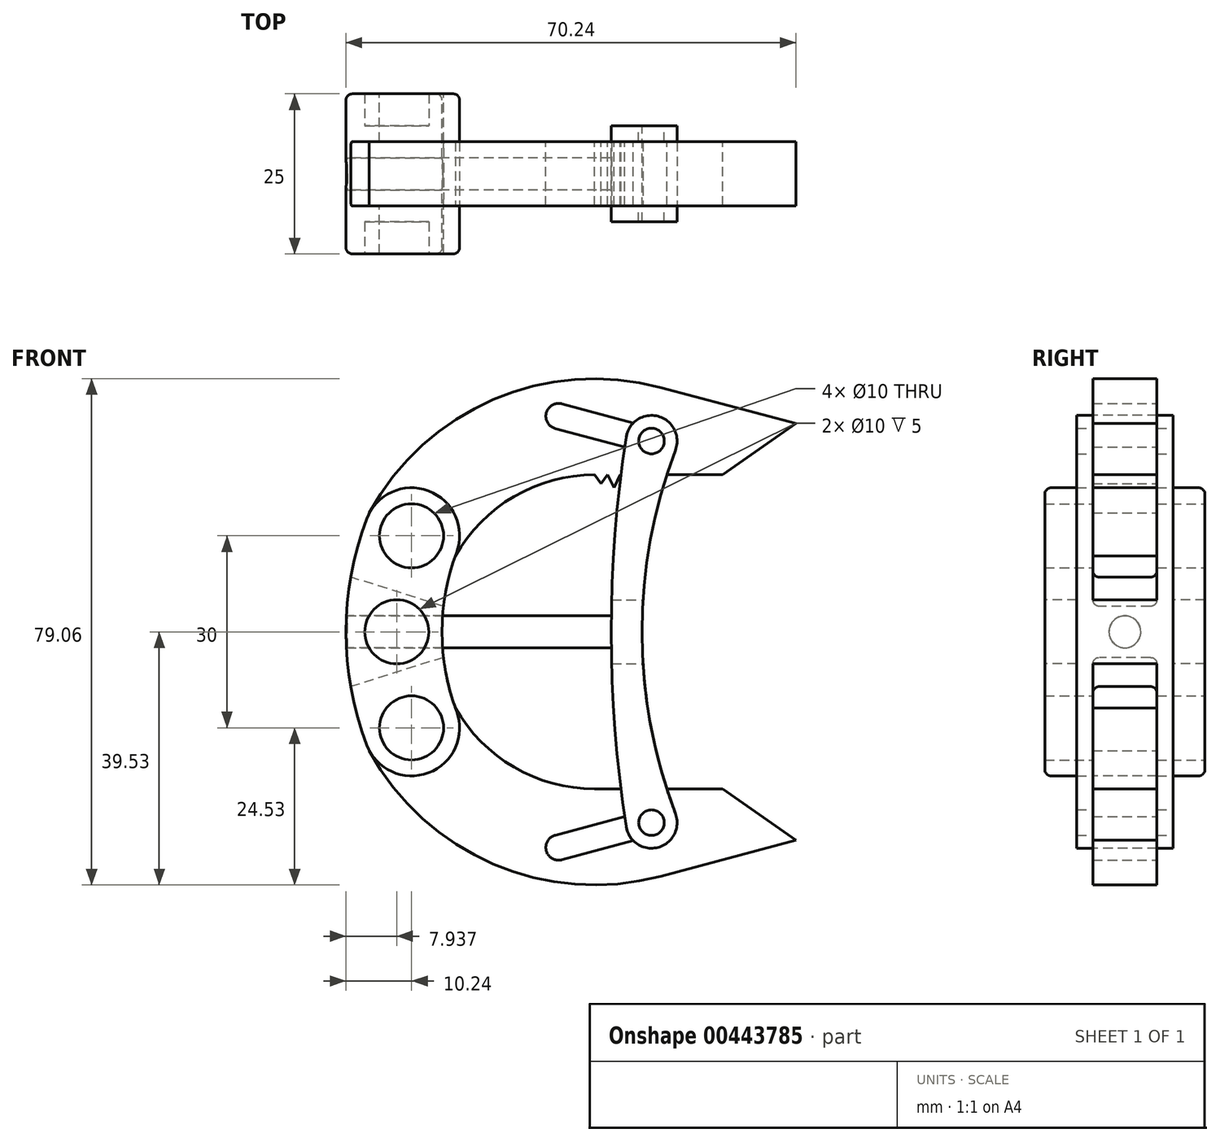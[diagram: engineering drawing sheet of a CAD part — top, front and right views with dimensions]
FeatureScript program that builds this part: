
annotation { "Feature Type Name" : "Feature", "Feature Type Description" : "" }
export const myFeature = defineFeature(function(context is Context, id is Id, definition is map)
    precondition{}
    {
        {
            var Q0;
            Q0=qCreatedBy(makeId("Front.planeOp"),FACE);
            var sketch = newSketch(context, id + "F0", { "sketchPlane" : qUnion([Q0])});
            skLineSegment(sketch, "E0", {"start": v(0, 15) * mm, "end": v(0, -15) * mm, "construction": true});
            skLineSegment(sketch, "E1", {"start": v(0, 0) * mm, "end": v(80, 0) * mm, "construction": true});
            skCircle(sketch, "E2", {"center": v(0, 15) * mm, "radius": 5 * mm});
            skCircle(sketch, "E3", {"center": v(0, -15) * mm, "radius": 5 * mm});
            skArc(sketch, "E4.0", {"start": v(7.02, 12.35) * mm, "mid": v(2.65, 22.02) * mm, "end": v(-7.02, 17.65) * mm});
            skArc(sketch, "E5.0", {"start": v(-7.02, -17.65) * mm, "mid": v(2.65, -22.02) * mm, "end": v(7.02, -12.35) * mm});
            skArc(sketch, "E6", {"start": v(-7.02, 17.65) * mm, "mid": v(-10.24, 0) * mm, "end": v(-7.02, -17.65) * mm});
            skArc(sketch, "E7", {"start": v(7.02, 12.35) * mm, "mid": v(4.76, 0) * mm, "end": v(7.02, -12.35) * mm});
            skSolve(sketch);
        }
        {
            var Q0;
            Q0=qCreatedBy(makeId("Front.planeOp"),FACE);
            var sketch = newSketch(context, id + "F1", { "sketchPlane" : qUnion([Q0])});
            skCircle(sketch, "E8.0", {"center": v(0, 15) * mm, "radius": 5 * mm});
            skArc(sketch, "E9", {"start": v(-6.6, 18.57) * mm, "mid": v(-3.57, 8.4) * mm, "end": v(6.6, 11.43) * mm});
            skArc(sketch, "E10", {"start": v(38.92, 38.17) * mm, "mid": v(12.76, 36.27) * mm, "end": v(-6.6, 18.57) * mm});
            skLineSegment(sketch, "E11", {"start": v(38.92, 38.17) * mm, "end": v(60, 32.53) * mm});
            skLineSegment(sketch, "E12", {"start": v(60, 32.53) * mm, "end": v(48.58, 24.53) * mm});
            skLineSegment(sketch, "E13", {"start": v(48.58, 24.53) * mm, "end": v(28.58, 24.53) * mm});
            skArc(sketch, "E14", {"start": v(28.58, 24.53) * mm, "mid": v(15.79, 21) * mm, "end": v(6.6, 11.43) * mm});
            skLineSegment(sketch, "E15", {"start": v(38.92, 38.17) * mm, "end": v(37.45, 29.8) * mm, "construction": true});
            skLineSegment(sketch, "E16", {"start": v(37.45, 29.8) * mm, "end": v(22.96, 33.68) * mm, "construction": true});
            skArc(sketch, "E17", {"start": v(23.48, 35.6) * mm, "mid": v(21.03, 34.2) * mm, "end": v(22.44, 31.75) * mm});
            skArc(sketch, "E18", {"start": v(36.93, 27.87) * mm, "mid": v(39.4, 29.37) * mm, "end": v(37.8, 31.77) * mm});
            skLineSegment(sketch, "E19", {"start": v(22.44, 31.75) * mm, "end": v(36.93, 27.87) * mm});
            skLineSegment(sketch, "E20", {"start": v(23.48, 35.6) * mm, "end": v(37.97, 31.73) * mm});
            skLineSegment(sketch, "E21.MirrorCS", {"start": v(23.48, -35.6) * mm, "end": v(37.97, -31.73) * mm});
            skLineSegment(sketch, "E22.MirrorCS", {"start": v(60, -32.53) * mm, "end": v(48.58, -24.53) * mm});
            skArc(sketch, "E23.MirrorCS", {"start": v(28.58, -24.53) * mm, "mid": v(15.79, -21) * mm, "end": v(6.6, -11.43) * mm});
            skLineSegment(sketch, "E24.MirrorCS", {"start": v(38.92, -38.17) * mm, "end": v(37.45, -29.8) * mm, "construction": true});
            skArc(sketch, "E25.MirrorC", {"start": v(-6.6, -18.57) * mm, "mid": v(-3.57, -8.4) * mm, "end": v(6.6, -11.43) * mm});
            skArc(sketch, "E26.MirrorCS", {"start": v(23.48, -35.6) * mm, "mid": v(21.03, -34.2) * mm, "end": v(22.44, -31.75) * mm});
            skLineSegment(sketch, "E27.MirrorCS", {"start": v(38.92, -38.17) * mm, "end": v(60, -32.53) * mm});
            skLineSegment(sketch, "E28.MirrorCS", {"start": v(22.44, -31.75) * mm, "end": v(36.93, -27.87) * mm});
            skLineSegment(sketch, "E29.MirrorCS", {"start": v(37.45, -29.8) * mm, "end": v(22.96, -33.68) * mm, "construction": true});
            skCircle(sketch, "E30.MirrorC", {"center": v(0, -15) * mm, "radius": 5 * mm});
            skArc(sketch, "E31.MirrorCS", {"start": v(38.92, -38.17) * mm, "mid": v(12.76, -36.27) * mm, "end": v(-6.6, -18.57) * mm});
            skArc(sketch, "E32.MirrorCS", {"start": v(36.93, -27.87) * mm, "mid": v(39.4, -29.37) * mm, "end": v(37.8, -31.77) * mm});
            skLineSegment(sketch, "E33.MirrorCS", {"start": v(48.58, -24.53) * mm, "end": v(28.58, -24.53) * mm});
            skLineSegment(sketch, "E34", {"start": v(28.58, 24.53) * mm, "end": v(29.6, 23.14) * mm});
            skLineSegment(sketch, "E35", {"start": v(29.6, 23.14) * mm, "end": v(30.58, 24.53) * mm});
            skLineSegment(sketch, "E36", {"start": v(30.58, 24.53) * mm, "end": v(31.6, 22.53) * mm});
            skLineSegment(sketch, "E37", {"start": v(31.6, 22.53) * mm, "end": v(32.58, 24.53) * mm});
            skLineSegment(sketch, "E38.1.0.0", {"start": v(32.6, 24.2) * mm, "end": v(33.62, 22.82) * mm});
            skLineSegment(sketch, "E38.1.0.1", {"start": v(33.62, 22.82) * mm, "end": v(34.6, 24.2) * mm});
            skLineSegment(sketch, "E38.1.0.2", {"start": v(34.6, 24.2) * mm, "end": v(35.62, 22.2) * mm});
            skLineSegment(sketch, "E38.1.0.3", {"start": v(35.62, 22.2) * mm, "end": v(36.6, 24.2) * mm});
            skLineSegment(sketch, "E38.2.0.0", {"start": v(36.63, 23.89) * mm, "end": v(37.64, 22.5) * mm});
            skLineSegment(sketch, "E38.2.0.1", {"start": v(37.64, 22.5) * mm, "end": v(38.63, 23.89) * mm});
            skLineSegment(sketch, "E38.2.0.2", {"start": v(38.63, 23.89) * mm, "end": v(39.64, 21.89) * mm});
            skLineSegment(sketch, "E38.2.0.3", {"start": v(39.64, 21.89) * mm, "end": v(40.63, 23.89) * mm});
            skLineSegment(sketch, "E38.3.0.0", {"start": v(40.66, 23.57) * mm, "end": v(41.67, 22.17) * mm});
            skLineSegment(sketch, "E38.3.0.1", {"start": v(41.67, 22.17) * mm, "end": v(42.66, 23.57) * mm});
            skLineSegment(sketch, "E38.3.0.2", {"start": v(42.66, 23.57) * mm, "end": v(43.67, 21.57) * mm});
            skLineSegment(sketch, "E38.3.0.3", {"start": v(43.67, 21.57) * mm, "end": v(44.66, 23.57) * mm});
            skLineSegment(sketch, "E38.4.0.0", {"start": v(44.68, 23.24) * mm, "end": v(45.7, 21.85) * mm});
            skLineSegment(sketch, "E38.4.0.1", {"start": v(45.7, 21.85) * mm, "end": v(46.68, 23.24) * mm});
            skLineSegment(sketch, "E38.4.0.2", {"start": v(46.68, 23.24) * mm, "end": v(47.7, 21.24) * mm});
            skLineSegment(sketch, "E38.4.0.3", {"start": v(47.7, 21.24) * mm, "end": v(48.68, 23.24) * mm});
            skLineSegment(sketch, "E38.direction1", {"start": v(29.6, 23.14) * mm, "end": v(33.62, 22.82) * mm, "construction": true});
            skSolve(sketch);
        }
        {
            var Q0;
            Q0 = qSketchRegion(id + "F1", true);
            extrude(context, id + "F2", {"entities" : qUnion([Q0]), "endBound" : BoundingType.SYMMETRIC, "depth" : 10 * mm});
        }
        {
            var Q0;
            Q0 = qSketchRegion(id + "F0", true);
            extrude(context, id + "F3", {"entities" : qUnion([Q0]), "endBound" : BoundingType.SYMMETRIC, "depth" : 25 * mm});
        }
        {
            var Q0;
            Q0=makeQuery(id+"F3.opExtrude","CAP_FACE",FACE,{"disambiguationData":[OSD([sQuery(id+"F0.wireOp",EDGE,"E2"),sQuery(id+"F0.wireOp",EDGE,"E3"),sQuery(id+"F0.wireOp",EDGE,"E4.0"),sQuery(id+"F0.wireOp",EDGE,"E5.0"),sQuery(id+"F0.wireOp",EDGE,"E6"),sQuery(id+"F0.wireOp",EDGE,"E7")])],"isStart":false});
            var sketch = newSketch(context, id + "F4", { "sketchPlane" : qUnion([Q0])});
            skArc(sketch, "E39", {"start": v(0, 15) * mm, "mid": v(-2.3, 0) * mm, "end": v(0, -15) * mm, "construction": true});
            skCircle(sketch, "E40", {"center": v(-2.3, 0) * mm, "radius": 5 * mm});
            skSolve(sketch);
        }
        {
            var Q0;
            Q0 = qSketchRegion(id + "F4", true);
            extrude(context, id + "F5", {"entities" : qUnion([Q0]), "operationType" : NewBodyOperationType.REMOVE, "endBound" : BoundingType.THROUGH_ALL, "oppositeDirection" : true, "depth" : 25 * mm});
        }
        {
            var Q0;
            Q0=qCreatedBy(makeId("Front.planeOp"),FACE);
            var sketch = newSketch(context, id + "F6", { "sketchPlane" : qUnion([Q0])});
            skArc(sketch, "E41.0", {"start": v(7.02, 12.35) * mm, "mid": v(2.65, 22.02) * mm, "end": v(-7.02, 17.65) * mm});
            skArc(sketch, "E41.1", {"start": v(-7.02, 17.65) * mm, "mid": v(-8.47, 13.16) * mm, "end": v(-9.5, 8.55) * mm});
            skCircle(sketch, "E41.2", {"center": v(0, 15) * mm, "radius": 5 * mm});
            skArc(sketch, "E41.3", {"start": v(7.02, 12.35) * mm, "mid": v(5.75, 8.24) * mm, "end": v(5, 4) * mm});
            skCircle(sketch, "E41.4", {"center": v(-2.3, 0) * mm, "radius": 5 * mm});
            skCircle(sketch, "E41.5", {"center": v(0, -15) * mm, "radius": 5 * mm});
            skArc(sketch, "E41.6", {"start": v(-7.02, -17.65) * mm, "mid": v(2.65, -22.02) * mm, "end": v(7.02, -12.35) * mm});
            skCircle(sketch, "E42.0", {"center": v(-2.3, 0) * mm, "radius": 6 * mm, "construction": true});
            skCircle(sketch, "E43", {"center": v(0, -15) * mm, "radius": 9 * mm, "construction": true});
            skLineSegment(sketch, "E44", {"start": v(5, -4) * mm, "end": v(5, -4) * mm});
            skLineSegment(sketch, "E45", {"start": v(5, 4) * mm, "end": v(-9.5, 8.55) * mm});
            skLineSegment(sketch, "E46", {"start": v(-2.3, 0) * mm, "end": v(19.17, 0) * mm, "construction": true});
            skArc(sketch, "E47", {"start": v(-9.5, 8.55) * mm, "mid": v(-10.24, 0) * mm, "end": v(-9.5, -8.55) * mm, "construction": true});
            skArc(sketch, "E48", {"start": v(-9.5, -8.55) * mm, "mid": v(-8.47, -13.16) * mm, "end": v(-7.02, -17.65) * mm});
            skLineSegment(sketch, "E49", {"start": v(5, -4) * mm, "end": v(-9.5, -8.55) * mm});
            skArc(sketch, "E50", {"start": v(5, 4) * mm, "mid": v(4.76, 0) * mm, "end": v(5, -4) * mm, "construction": true});
            skArc(sketch, "E51", {"start": v(5, -4) * mm, "mid": v(5.75, -8.24) * mm, "end": v(7.02, -12.35) * mm});
            skSolve(sketch);
        }
        {
            var Q0;
            Q0 = qSketchRegion(id + "F6", true);
            extrude(context, id + "F7", {"entities" : qUnion([Q0]), "operationType" : NewBodyOperationType.REMOVE, "endBound" : BoundingType.SYMMETRIC, "oppositeDirection" : true, "depth" : 10 * mm});
        }
        {
            var Q0;
            Q0=qCreatedBy(makeId("Front.planeOp"),FACE);
            var sketch = newSketch(context, id + "F8", { "sketchPlane" : qUnion([Q0])});
            skCircle(sketch, "E52.1.0", {"center": v(-2.3, 0) * mm, "radius": 5 * mm});
            skSolve(sketch);
        }
        {
            var Q0;
            Q0 = qSketchRegion(id + "F8", true);
            extrude(context, id + "F9", {"entities" : qUnion([Q0]), "operationType" : NewBodyOperationType.ADD, "endBound" : BoundingType.SYMMETRIC, "depth" : 15 * mm});
        }
        {
            var Q0;
            Q0=qCreatedBy(makeId("Right.planeOp"),FACE);
            var sketch = newSketch(context, id + "F10", { "sketchPlane" : qUnion([Q0])});
            skCircle(sketch, "E53", {"center": v(0, 0) * mm, "radius": 2.5 * mm});
            skSolve(sketch);
        }
        {
            var Q0;
            Q0 = qSketchRegion(id + "F10", true);
            extrude(context, id + "F11", {"entities" : qUnion([Q0]), "operationType" : NewBodyOperationType.REMOVE, "endBound" : BoundingType.THROUGH_ALL, "oppositeDirection" : true, "depth" : 25 * mm, "hasSecondDirection" : true, "secondDirectionBound" : SecondDirectionBoundingType.THROUGH_ALL, "secondDirectionOppositeDirection" : false, "secondDirectionDepth" : 25 * mm});
        }
        {
            var Q0;
            Q0=qCreatedBy(makeId("Right.planeOp"),FACE);
            var sketch = newSketch(context, id + "F12", { "sketchPlane" : qUnion([Q0])});
            skCircle(sketch, "E54.0", {"center": v(0, 0) * mm, "radius": 2.5 * mm});
            skSolve(sketch);
        }
        {
            var Q0;
            Q0 = qSketchRegion(id + "F12", true);
            extrude(context, id + "F13", {"entities" : qUnion([Q0]), "depth" : 32 * mm, "hasSecondDirection" : true, "secondDirectionOppositeDirection" : true, "secondDirectionDepth" : 10 * mm});
        }
        {
            var Q0;
            Q0=qCreatedBy(makeId("Front.planeOp"),FACE);
            var sketch = newSketch(context, id + "F14", { "sketchPlane" : qUnion([Q0])});
            skArc(sketch, "E55.0", {"start": v(36.93, 27.87) * mm, "mid": v(39.38, 29.28) * mm, "end": v(37.97, 31.73) * mm});
            skArc(sketch, "E55.1", {"start": v(36.93, -27.87) * mm, "mid": v(39.38, -29.28) * mm, "end": v(37.97, -31.73) * mm});
            skCircle(sketch, "E56", {"center": v(37.45, 29.8) * mm, "radius": 2 * mm});
            skCircle(sketch, "E57", {"center": v(37.45, -29.8) * mm, "radius": 2 * mm});
            skCircle(sketch, "E58", {"center": v(37.45, 29.8) * mm, "radius": 4 * mm});
            skCircle(sketch, "E59", {"center": v(37.45, -29.8) * mm, "radius": 4 * mm});
            skArc(sketch, "E60", {"start": v(33.5, 30.4) * mm, "mid": v(31.17, 0) * mm, "end": v(33.5, -30.4) * mm});
            skArc(sketch, "E61", {"start": v(41.19, 28.38) * mm, "mid": v(35.99, 0) * mm, "end": v(41.19, -28.38) * mm});
            skSolve(sketch);
        }
        {
            var Q0;
            Q0 = qSketchRegion(id + "F14", true);
            extrude(context, id + "F15", {"entities" : qUnion([Q0]), "operationType" : NewBodyOperationType.ADD, "endBound" : BoundingType.SYMMETRIC, "depth" : 15 * mm});
        }
        {
            var Q0;
            Q0=qCreatedBy(makeId("Front.planeOp"),FACE);
            var sketch = newSketch(context, id + "F16", { "sketchPlane" : qUnion([Q0])});
            skArc(sketch, "E62.0", {"start": v(33.5, 30.4) * mm, "mid": v(31.96, 17.74) * mm, "end": v(31.23, 5) * mm});
            skArc(sketch, "E62.1", {"start": v(41.19, 28.38) * mm, "mid": v(38.47, 33.67) * mm, "end": v(33.5, 30.4) * mm});
            skArc(sketch, "E62.2", {"start": v(33.5, -30.4) * mm, "mid": v(38.47, -33.67) * mm, "end": v(41.19, -28.38) * mm});
            skArc(sketch, "E62.3", {"start": v(41.19, 28.38) * mm, "mid": v(37.79, 16.88) * mm, "end": v(36.14, 5) * mm});
            skPoint(sketch, "E62.4", {"position": v(38.47, -33.67) * mm});
            skLineSegment(sketch, "E63", {"start": v(31.23, 5) * mm, "end": v(36.14, 5) * mm});
            skLineSegment(sketch, "E64", {"start": v(31.23, -5) * mm, "end": v(36.14, -5) * mm});
            skArc(sketch, "E65", {"start": v(31.23, 5) * mm, "mid": v(31.17, 0) * mm, "end": v(31.23, -5) * mm, "construction": true});
            skArc(sketch, "E66", {"start": v(31.23, -5) * mm, "mid": v(31.96, -17.74) * mm, "end": v(33.5, -30.4) * mm});
            skLineSegment(sketch, "E67", {"start": v(36.14, -5) * mm, "end": v(36.14, -5) * mm});
            skArc(sketch, "E68", {"start": v(36.14, 5) * mm, "mid": v(35.99, 0) * mm, "end": v(36.14, -5) * mm, "construction": true});
            skArc(sketch, "E69", {"start": v(36.14, -5) * mm, "mid": v(37.79, -16.88) * mm, "end": v(41.19, -28.38) * mm});
            skSolve(sketch);
        }
        {
            var Q0;
            Q0 = qSketchRegion(id + "F16", true);
            extrude(context, id + "F17", {"entities" : qUnion([Q0]), "operationType" : NewBodyOperationType.REMOVE, "endBound" : BoundingType.SYMMETRIC, "oppositeDirection" : true, "depth" : 10 * mm});
        }
        {
            var Q0;
            Q0=makeQuery(id+"F3.opExtrude","CAP_EDGE",EDGE,{"disambiguationData":[OSD([sQuery(id+"F0.wireOp",EDGE,"E7")])],"isStart":false});
            var Q1;
            Q1=makeQuery(id+"F3.opExtrude","CAP_EDGE",EDGE,{"disambiguationData":[OSD([sQuery(id+"F0.wireOp",EDGE,"E7")])],"isStart":true});
            var Q2;
            Q2=makeQuery(id+"F7.boolean.opBoolean","COPY",EDGE,{"derivedFrom":makeQuery(id+"F7.opExtrude","SWEPT_EDGE",EDGE,{"disambiguationData":[OSD([sQuery(id+"F6.wireOp",EDGE,"E49"),sQuery(id+"F6.wireOp",EDGE,"E51")])]})});
            var Q3;
            Q3=makeQuery(id+"F7.boolean.opBoolean","COPY",EDGE,{"derivedFrom":makeQuery(id+"F7.opExtrude","SWEPT_EDGE",EDGE,{"disambiguationData":[OSD([sQuery(id+"F6.wireOp",EDGE,"E41.3"),sQuery(id+"F6.wireOp",EDGE,"E45")])]})});
            var Q4;
            Q4=makeQuery(id+"F7.boolean.opBoolean","COPY",EDGE,{"derivedFrom":makeQuery(id+"F7.opExtrude","CAP_EDGE",EDGE,{"disambiguationData":[OSD([sQuery(id+"F6.wireOp",EDGE,"E49")])],"isStart":false})});
            var Q5;
            Q5=makeQuery(id+"F7.boolean.opBoolean","COPY",EDGE,{"derivedFrom":makeQuery(id+"F7.opExtrude","CAP_EDGE",EDGE,{"disambiguationData":[OSD([sQuery(id+"F6.wireOp",EDGE,"E45")])],"isStart":false})});
            var Q6;
            Q6=makeQuery(id+"F7.boolean.opBoolean","COPY",EDGE,{"derivedFrom":makeQuery(id+"F7.opExtrude","CAP_EDGE",EDGE,{"disambiguationData":[OSD([sQuery(id+"F6.wireOp",EDGE,"E45")])],"isStart":true})});
            var Q7;
            Q7=makeQuery(id+"F7.boolean.opBoolean","COPY",EDGE,{"derivedFrom":makeQuery(id+"F7.opExtrude","CAP_EDGE",EDGE,{"disambiguationData":[OSD([sQuery(id+"F6.wireOp",EDGE,"E49")])],"isStart":true})});
            fillet(context, id + "F18", {"entities" : qUnion([Q0, Q1, Q2, Q3, Q4, Q5, Q6, Q7]), "radius" : 1 * mm, "tangentPropagation" : true, "allowEdgeOverflow" : false});
        }
    });
